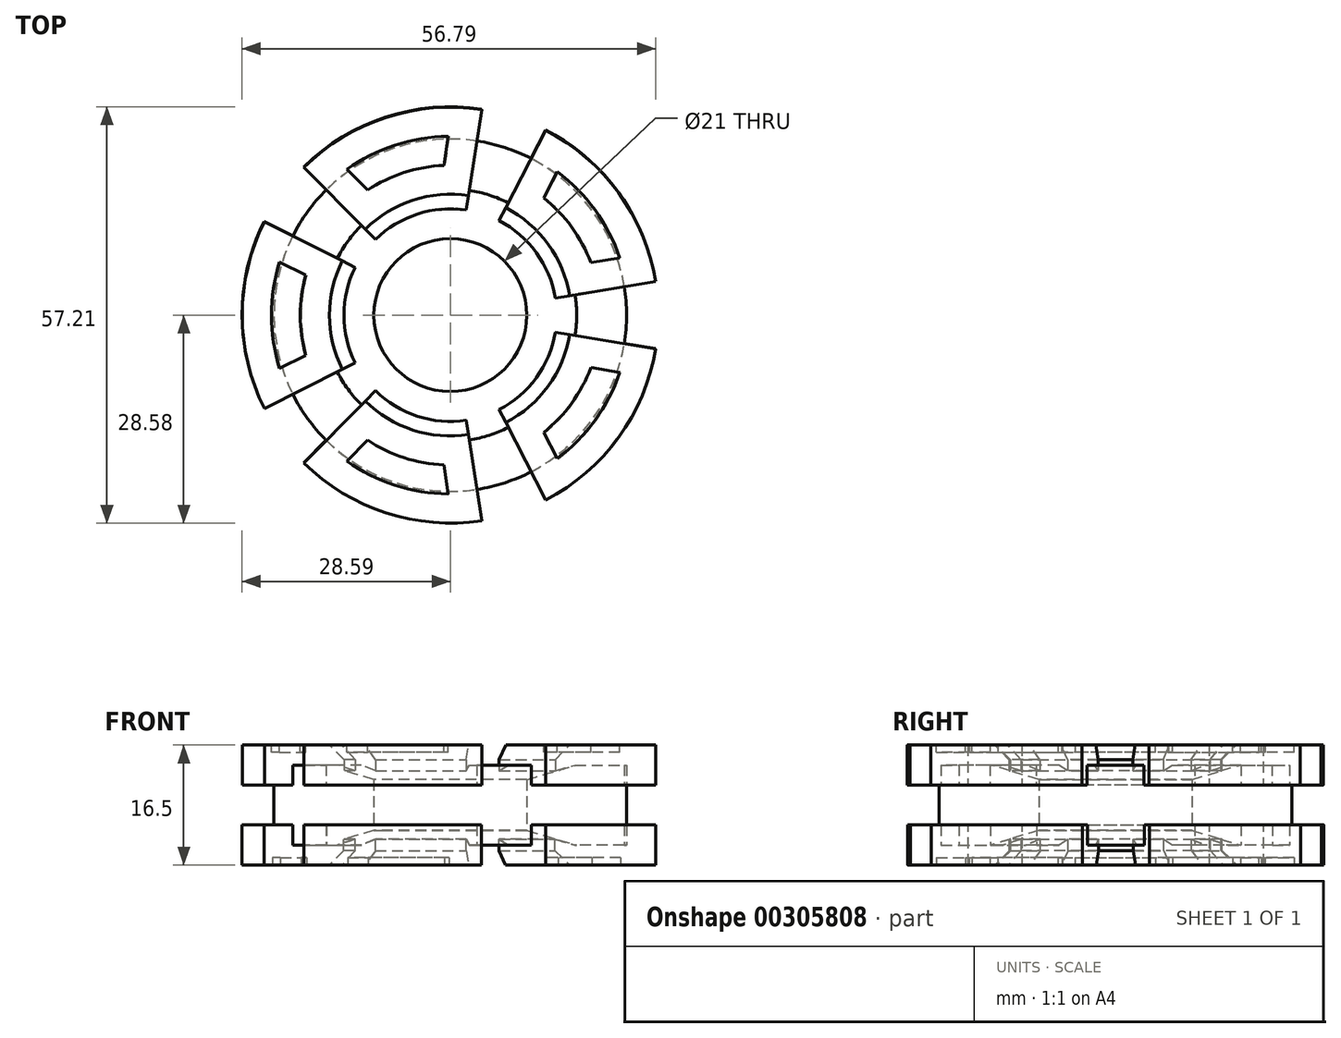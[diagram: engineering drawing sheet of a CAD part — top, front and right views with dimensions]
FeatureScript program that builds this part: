
annotation { "Feature Type Name" : "Feature", "Feature Type Description" : "" }
export const myFeature = defineFeature(function(context is Context, id is Id, definition is map)
    precondition{}
    {
        {
            var Q0;
            Q0=qCreatedBy(makeId("Top.planeOp"),FACE);
            var sketch = newSketch(context, id + "F0", { "sketchPlane" : qUnion([Q0])});
            skCircle(sketch, "E0", {"center": v(0, 0) * mm, "radius": 10.5 * mm});
            skCircle(sketch, "E1.0", {"center": v(0, 0) * mm, "radius": 24.22 * mm});
            skSolve(sketch);
        }
        {
            var Q0;
            Q0 = qSketchRegion(id + "F0", true);
            extrude(context, id + "F1", {"entities" : qUnion([Q0]), "depth" : 11 * mm});
        }
        {
            var Q0;
            Q0=makeQuery(id+"F1.opExtrude","CAP_EDGE",EDGE,{"disambiguationData":[OSD([sQuery(id+"F0.wireOp",EDGE,"E0")])],"isStart":false});
            chamfer(context, id + "F2", {"entities" : qUnion([Q0]), "chamferType" : ChamferType.TWO_OFFSETS, "width1" : 2 * mm, "oppositeDirection" : false, "width2" : 6.86 * mm, "tangentPropagation" : true});
        }
        {
            var Q0;
            Q0=makeQuery(id+"F1.opExtrude","CAP_EDGE",EDGE,{"disambiguationData":[OSD([sQuery(id+"F0.wireOp",EDGE,"E0")])],"isStart":true});
            chamfer(context, id + "F3", {"entities" : qUnion([Q0]), "chamferType" : ChamferType.TWO_OFFSETS, "width1" : 6.86 * mm, "oppositeDirection" : false, "width2" : 2 * mm, "tangentPropagation" : true});
        }
        {
            var Q0;
            Q0=makeQuery(id+"F1.opExtrude","CAP_FACE",FACE,{"disambiguationData":[OSD([sQuery(id+"F0.wireOp",EDGE,"E0"),sQuery(id+"F0.wireOp",EDGE,"E1.0")])],"isStart":false});
            var sketch = newSketch(context, id + "F4", { "sketchPlane" : qUnion([Q0])});
            skArc(sketch, "E2", {"start": v(-25.53, 12.84) * mm, "mid": v(-28.58, 0) * mm, "end": v(-25.53, -12.84) * mm});
            skArc(sketch, "E3", {"start": v(-13.05, 6.56) * mm, "mid": v(-14.6, 0) * mm, "end": v(-13.05, -6.56) * mm});
            skPoint(sketch, "E4.start.orphan", {"position": v(-29.77, 0) * mm});
            skLineSegment(sketch, "E5", {"start": v(-25.53, 12.84) * mm, "end": v(-13.05, 6.56) * mm});
            skLineSegment(sketch, "E6", {"start": v(-25.53, -12.84) * mm, "end": v(-13.05, -6.56) * mm});
            skPoint(sketch, "E7.1.0", {"position": v(-9.2, -28.31) * mm});
            skLineSegment(sketch, "E7.1.1", {"start": v(4.32, -28.25) * mm, "end": v(2.2, -14.44) * mm});
            skLineSegment(sketch, "E7.1.2", {"start": v(-20.1, -20.31) * mm, "end": v(-10.27, -10.38) * mm});
            skArc(sketch, "E7.1.3", {"start": v(-10.27, -10.38) * mm, "mid": v(-4.51, -13.9) * mm, "end": v(2.2, -14.44) * mm});
            skArc(sketch, "E7.1.4", {"start": v(-20.1, -20.31) * mm, "mid": v(-8.83, -27.18) * mm, "end": v(4.32, -28.25) * mm});
            skPoint(sketch, "E7.2.0", {"position": v(24.08, -17.5) * mm});
            skLineSegment(sketch, "E7.2.1", {"start": v(28.2, -4.62) * mm, "end": v(14.41, -2.36) * mm});
            skLineSegment(sketch, "E7.2.2", {"start": v(13.1, -25.4) * mm, "end": v(6.7, -12.98) * mm});
            skArc(sketch, "E7.2.3", {"start": v(6.7, -12.98) * mm, "mid": v(11.82, -8.58) * mm, "end": v(14.41, -2.36) * mm});
            skArc(sketch, "E7.2.4", {"start": v(13.1, -25.4) * mm, "mid": v(23.12, -16.8) * mm, "end": v(28.2, -4.62) * mm});
            skPoint(sketch, "E7.3.0", {"position": v(24.08, 17.5) * mm});
            skLineSegment(sketch, "E7.3.1", {"start": v(13.1, 25.4) * mm, "end": v(6.7, 12.98) * mm});
            skLineSegment(sketch, "E7.3.2", {"start": v(28.2, 4.62) * mm, "end": v(14.41, 2.36) * mm});
            skArc(sketch, "E7.3.3", {"start": v(14.41, 2.36) * mm, "mid": v(11.82, 8.58) * mm, "end": v(6.7, 12.98) * mm});
            skArc(sketch, "E7.3.4", {"start": v(28.2, 4.62) * mm, "mid": v(23.12, 16.8) * mm, "end": v(13.1, 25.4) * mm});
            skPoint(sketch, "E7.4.0", {"position": v(-9.2, 28.31) * mm});
            skLineSegment(sketch, "E7.4.1", {"start": v(-20.1, 20.31) * mm, "end": v(-10.27, 10.38) * mm});
            skLineSegment(sketch, "E7.4.2", {"start": v(4.32, 28.25) * mm, "end": v(2.2, 14.44) * mm});
            skArc(sketch, "E7.4.3", {"start": v(2.2, 14.44) * mm, "mid": v(-4.51, 13.9) * mm, "end": v(-10.27, 10.38) * mm});
            skArc(sketch, "E7.4.4", {"start": v(4.32, 28.25) * mm, "mid": v(-8.83, 27.18) * mm, "end": v(-20.1, 20.31) * mm});
            skSolve(sketch);
        }
        {
            var Q0;
            Q0 = qSketchRegion(id + "F4", true);
            extrude(context, id + "F5", {"entities" : qUnion([Q0]), "operationType" : NewBodyOperationType.ADD, "endBound" : BoundingType.SYMMETRIC, "depth" : 5.5 * mm});
        }
        {
            var Q0;
            Q0=makeQuery(id+"F5.opExtrude","CAP_EDGE",EDGE,{"disambiguationData":[OSD([sQuery(id+"F4.wireOp",EDGE,"E7.4.3")])],"isStart":false});
            chamfer(context, id + "F6", {"entities" : qUnion([Q0]), "width" : 2 * mm, "tangentPropagation" : true});
        }
        {
            var Q0;
            Q0=makeQuery(id+"F5.opExtrude","CAP_EDGE",EDGE,{"disambiguationData":[OSD([sQuery(id+"F4.wireOp",EDGE,"E3")])],"isStart":false});
            var Q1;
            Q1=makeQuery(id+"F5.opExtrude","CAP_EDGE",EDGE,{"disambiguationData":[OSD([sQuery(id+"F4.wireOp",EDGE,"E7.1.3")])],"isStart":false});
            var Q2;
            Q2=makeQuery(id+"F5.opExtrude","CAP_EDGE",EDGE,{"disambiguationData":[OSD([sQuery(id+"F4.wireOp",EDGE,"E7.2.3")])],"isStart":false});
            var Q3;
            Q3=makeQuery(id+"F5.opExtrude","CAP_EDGE",EDGE,{"disambiguationData":[OSD([sQuery(id+"F4.wireOp",EDGE,"E7.3.3")])],"isStart":false});
            chamfer(context, id + "F7", {"entities" : qUnion([Q0, Q1, Q2, Q3]), "width" : 2 * mm, "tangentPropagation" : true});
        }
        {
            var Q0;
            Q0=makeQuery(id+"F1.opExtrude","CAP_FACE",FACE,{"disambiguationData":[OSD([sQuery(id+"F0.wireOp",EDGE,"E0"),sQuery(id+"F0.wireOp",EDGE,"E1.0")])],"isStart":true});
            var sketch = newSketch(context, id + "F8", { "sketchPlane" : qUnion([Q0])});
            skArc(sketch, "E8", {"start": v(-25.55, 12.78) * mm, "mid": v(-28.6, -0.06) * mm, "end": v(-25.55, -12.9) * mm});
            skArc(sketch, "E9", {"start": v(-13.07, 6.5) * mm, "mid": v(-14.62, -0.06) * mm, "end": v(-13.07, -6.62) * mm});
            skPoint(sketch, "E10.start.orphan", {"position": v(-29.79, -0.06) * mm});
            skLineSegment(sketch, "E11", {"start": v(-25.55, 12.78) * mm, "end": v(-13.07, 6.5) * mm});
            skLineSegment(sketch, "E12", {"start": v(-25.55, -12.9) * mm, "end": v(-13.07, -6.62) * mm});
            skPoint(sketch, "E13.1.0", {"position": v(-9.22, -28.37) * mm});
            skLineSegment(sketch, "E13.1.1", {"start": v(4.3, -28.3) * mm, "end": v(2.2, -14.5) * mm});
            skLineSegment(sketch, "E13.1.2", {"start": v(-20.11, -20.37) * mm, "end": v(-10.29, -10.44) * mm});
            skArc(sketch, "E13.1.3", {"start": v(-10.29, -10.44) * mm, "mid": v(-4.53, -13.95) * mm, "end": v(2.2, -14.5) * mm});
            skArc(sketch, "E13.1.4", {"start": v(-20.11, -20.37) * mm, "mid": v(-8.85, -27.24) * mm, "end": v(4.3, -28.3) * mm});
            skPoint(sketch, "E13.2.0", {"position": v(24.07, -17.56) * mm});
            skLineSegment(sketch, "E13.2.1", {"start": v(28.18, -4.68) * mm, "end": v(14.4, -2.42) * mm});
            skLineSegment(sketch, "E13.2.2", {"start": v(13.1, -25.45) * mm, "end": v(6.68, -13.04) * mm});
            skArc(sketch, "E13.2.3", {"start": v(6.68, -13.04) * mm, "mid": v(11.8, -8.64) * mm, "end": v(14.4, -2.42) * mm});
            skArc(sketch, "E13.2.4", {"start": v(13.1, -25.45) * mm, "mid": v(23.1, -16.86) * mm, "end": v(28.18, -4.68) * mm});
            skPoint(sketch, "E13.3.0", {"position": v(24.07, 17.44) * mm});
            skLineSegment(sketch, "E13.3.1", {"start": v(13.1, 25.33) * mm, "end": v(6.68, 12.92) * mm});
            skLineSegment(sketch, "E13.3.2", {"start": v(28.18, 4.56) * mm, "end": v(14.4, 2.3) * mm});
            skArc(sketch, "E13.3.3", {"start": v(14.4, 2.3) * mm, "mid": v(11.8, 8.52) * mm, "end": v(6.68, 12.92) * mm});
            skArc(sketch, "E13.3.4", {"start": v(28.18, 4.56) * mm, "mid": v(23.1, 16.74) * mm, "end": v(13.1, 25.33) * mm});
            skPoint(sketch, "E13.4.0", {"position": v(-9.22, 28.25) * mm});
            skLineSegment(sketch, "E13.4.1", {"start": v(-20.11, 20.25) * mm, "end": v(-10.29, 10.32) * mm});
            skLineSegment(sketch, "E13.4.2", {"start": v(4.3, 28.19) * mm, "end": v(2.2, 14.38) * mm});
            skArc(sketch, "E13.4.3", {"start": v(2.2, 14.38) * mm, "mid": v(-4.53, 13.83) * mm, "end": v(-10.29, 10.32) * mm});
            skArc(sketch, "E13.4.4", {"start": v(4.3, 28.19) * mm, "mid": v(-8.85, 27.12) * mm, "end": v(-20.11, 20.25) * mm});
            skSolve(sketch);
        }
        {
            var Q0;
            Q0 = qSketchRegion(id + "F8", true);
            extrude(context, id + "F9", {"entities" : qUnion([Q0]), "operationType" : NewBodyOperationType.ADD, "endBound" : BoundingType.SYMMETRIC, "depth" : 5.5 * mm});
        }
        {
            var Q0;
            Q0=makeQuery(id+"F9.opExtrude","CAP_EDGE",EDGE,{"disambiguationData":[OSD([sQuery(id+"F8.wireOp",EDGE,"E13.4.3")])],"isStart":false});
            var Q1;
            Q1=makeQuery(id+"F9.opExtrude","CAP_EDGE",EDGE,{"disambiguationData":[OSD([sQuery(id+"F8.wireOp",EDGE,"E9")])],"isStart":false});
            var Q2;
            Q2=makeQuery(id+"F9.opExtrude","CAP_EDGE",EDGE,{"disambiguationData":[OSD([sQuery(id+"F8.wireOp",EDGE,"E13.1.3")])],"isStart":false});
            var Q3;
            Q3=makeQuery(id+"F9.opExtrude","CAP_EDGE",EDGE,{"disambiguationData":[OSD([sQuery(id+"F8.wireOp",EDGE,"E13.2.3")])],"isStart":false});
            var Q4;
            Q4=makeQuery(id+"F9.opExtrude","CAP_EDGE",EDGE,{"disambiguationData":[OSD([sQuery(id+"F8.wireOp",EDGE,"E13.3.3")])],"isStart":false});
            chamfer(context, id + "F10", {"entities" : qUnion([Q0, Q1, Q2, Q3, Q4]), "width" : 2 * mm, "tangentPropagation" : true});
        }
        {
            var Q0;
            Q0=makeQuery(id+"F5.opExtrude","CAP_FACE",FACE,{"disambiguationData":[OSD([sQuery(id+"F4.wireOp",EDGE,"E2"),sQuery(id+"F4.wireOp",EDGE,"E3"),sQuery(id+"F4.wireOp",EDGE,"E5"),sQuery(id+"F4.wireOp",EDGE,"E6")])],"isStart":false});
            var sketch = newSketch(context, id + "F11", { "sketchPlane" : qUnion([Q0])});
            skLineSegment(sketch, "E14.0", {"start": v(-23.46, 7.32) * mm, "end": v(-19.86, 5.5) * mm});
            skArc(sketch, "E15.0", {"start": v(-23.46, 7.32) * mm, "mid": v(-24.58, 0) * mm, "end": v(-23.46, -7.32) * mm});
            skArc(sketch, "E16.0", {"start": v(-19.86, -5.5) * mm, "mid": v(-20.6, 0) * mm, "end": v(-19.86, 5.5) * mm});
            skLineSegment(sketch, "E17.0", {"start": v(-23.46, -7.32) * mm, "end": v(-19.86, -5.5) * mm});
            skLineSegment(sketch, "E18.1.0", {"start": v(-14.21, -20.05) * mm, "end": v(-11.37, -17.18) * mm});
            skArc(sketch, "E18.1.1", {"start": v(-14.21, -20.05) * mm, "mid": v(-7.6, -23.37) * mm, "end": v(-0.29, -24.57) * mm});
            skArc(sketch, "E18.1.2", {"start": v(-0.9, -20.59) * mm, "mid": v(-6.37, -19.6) * mm, "end": v(-11.37, -17.18) * mm});
            skLineSegment(sketch, "E18.1.3", {"start": v(-0.29, -24.57) * mm, "end": v(-0.9, -20.59) * mm});
            skLineSegment(sketch, "E18.2.0", {"start": v(14.68, -19.71) * mm, "end": v(12.83, -16.13) * mm});
            skArc(sketch, "E18.2.1", {"start": v(14.68, -19.71) * mm, "mid": v(19.88, -14.44) * mm, "end": v(23.28, -7.87) * mm});
            skArc(sketch, "E18.2.2", {"start": v(19.3, -7.22) * mm, "mid": v(16.67, -12.11) * mm, "end": v(12.83, -16.13) * mm});
            skLineSegment(sketch, "E18.2.3", {"start": v(23.28, -7.87) * mm, "end": v(19.3, -7.22) * mm});
            skLineSegment(sketch, "E18.3.0", {"start": v(23.28, 7.87) * mm, "end": v(19.3, 7.22) * mm});
            skArc(sketch, "E18.3.1", {"start": v(23.28, 7.87) * mm, "mid": v(19.88, 14.44) * mm, "end": v(14.68, 19.71) * mm});
            skArc(sketch, "E18.3.2", {"start": v(12.83, 16.13) * mm, "mid": v(16.67, 12.11) * mm, "end": v(19.3, 7.22) * mm});
            skLineSegment(sketch, "E18.3.3", {"start": v(14.68, 19.71) * mm, "end": v(12.83, 16.13) * mm});
            skLineSegment(sketch, "E18.4.0", {"start": v(-0.29, 24.57) * mm, "end": v(-0.9, 20.59) * mm});
            skArc(sketch, "E18.4.1", {"start": v(-0.29, 24.57) * mm, "mid": v(-7.6, 23.37) * mm, "end": v(-14.21, 20.05) * mm});
            skArc(sketch, "E18.4.2", {"start": v(-11.37, 17.18) * mm, "mid": v(-6.37, 19.6) * mm, "end": v(-0.9, 20.59) * mm});
            skLineSegment(sketch, "E18.4.3", {"start": v(-14.21, 20.05) * mm, "end": v(-11.37, 17.18) * mm});
            skSolve(sketch);
        }
        {
            var Q0;
            Q0 = qSketchRegion(id + "F11", true);
            extrude(context, id + "F12", {"entities" : qUnion([Q0]), "operationType" : NewBodyOperationType.REMOVE, "oppositeDirection" : true, "depth" : 1 * mm});
        }
        {
            var Q0;
            Q0=makeQuery(id+"F9.opExtrude","CAP_FACE",FACE,{"disambiguationData":[OSD([sQuery(id+"F8.wireOp",EDGE,"E8"),sQuery(id+"F8.wireOp",EDGE,"E9"),sQuery(id+"F8.wireOp",EDGE,"E11"),sQuery(id+"F8.wireOp",EDGE,"E12")])],"isStart":false});
            var sketch = newSketch(context, id + "F13", { "sketchPlane" : qUnion([Q0])});
            skLineSegment(sketch, "E19.0", {"start": v(-23.34, 7.34) * mm, "end": v(-19.74, 5.53) * mm});
            skArc(sketch, "E20.0", {"start": v(-23.34, 7.34) * mm, "mid": v(-24.46, 0.02) * mm, "end": v(-23.34, -7.3) * mm});
            skArc(sketch, "E21.0", {"start": v(-19.74, -5.48) * mm, "mid": v(-20.49, 0.02) * mm, "end": v(-19.74, 5.53) * mm});
            skLineSegment(sketch, "E22.0", {"start": v(-23.34, -7.3) * mm, "end": v(-19.74, -5.48) * mm});
            skLineSegment(sketch, "E23.1.0", {"start": v(-14.1, -20.03) * mm, "end": v(-11.25, -17.16) * mm});
            skArc(sketch, "E23.1.1", {"start": v(-14.1, -20.03) * mm, "mid": v(-7.47, -23.35) * mm, "end": v(-0.17, -24.55) * mm});
            skArc(sketch, "E23.1.2", {"start": v(-0.78, -20.56) * mm, "mid": v(-6.25, -19.57) * mm, "end": v(-11.25, -17.16) * mm});
            skLineSegment(sketch, "E23.1.3", {"start": v(-0.17, -24.55) * mm, "end": v(-0.78, -20.56) * mm});
            skLineSegment(sketch, "E23.2.0", {"start": v(14.8, -19.69) * mm, "end": v(12.95, -16.1) * mm});
            skArc(sketch, "E23.2.1", {"start": v(14.8, -19.69) * mm, "mid": v(20, -14.42) * mm, "end": v(23.4, -7.84) * mm});
            skArc(sketch, "E23.2.2", {"start": v(19.42, -7.2) * mm, "mid": v(16.79, -12.09) * mm, "end": v(12.95, -16.1) * mm});
            skLineSegment(sketch, "E23.2.3", {"start": v(23.4, -7.84) * mm, "end": v(19.42, -7.2) * mm});
            skLineSegment(sketch, "E23.3.0", {"start": v(23.4, 7.9) * mm, "end": v(19.42, 7.24) * mm});
            skArc(sketch, "E23.3.1", {"start": v(23.4, 7.9) * mm, "mid": v(20, 14.47) * mm, "end": v(14.8, 19.73) * mm});
            skArc(sketch, "E23.3.2", {"start": v(12.95, 16.15) * mm, "mid": v(16.79, 12.14) * mm, "end": v(19.42, 7.24) * mm});
            skLineSegment(sketch, "E23.3.3", {"start": v(14.8, 19.73) * mm, "end": v(12.95, 16.15) * mm});
            skLineSegment(sketch, "E23.4.0", {"start": v(-0.17, 24.6) * mm, "end": v(-0.78, 20.6) * mm});
            skArc(sketch, "E23.4.1", {"start": v(-0.17, 24.6) * mm, "mid": v(-7.47, 23.4) * mm, "end": v(-14.1, 20.07) * mm});
            skArc(sketch, "E23.4.2", {"start": v(-11.25, 17.2) * mm, "mid": v(-6.25, 19.62) * mm, "end": v(-0.78, 20.6) * mm});
            skLineSegment(sketch, "E23.4.3", {"start": v(-14.1, 20.07) * mm, "end": v(-11.25, 17.2) * mm});
            skSolve(sketch);
        }
        {
            var Q0;
            Q0 = qSketchRegion(id + "F13", true);
            extrude(context, id + "F14", {"entities" : qUnion([Q0]), "operationType" : NewBodyOperationType.REMOVE, "oppositeDirection" : true, "depth" : 1 * mm});
        }
    });
